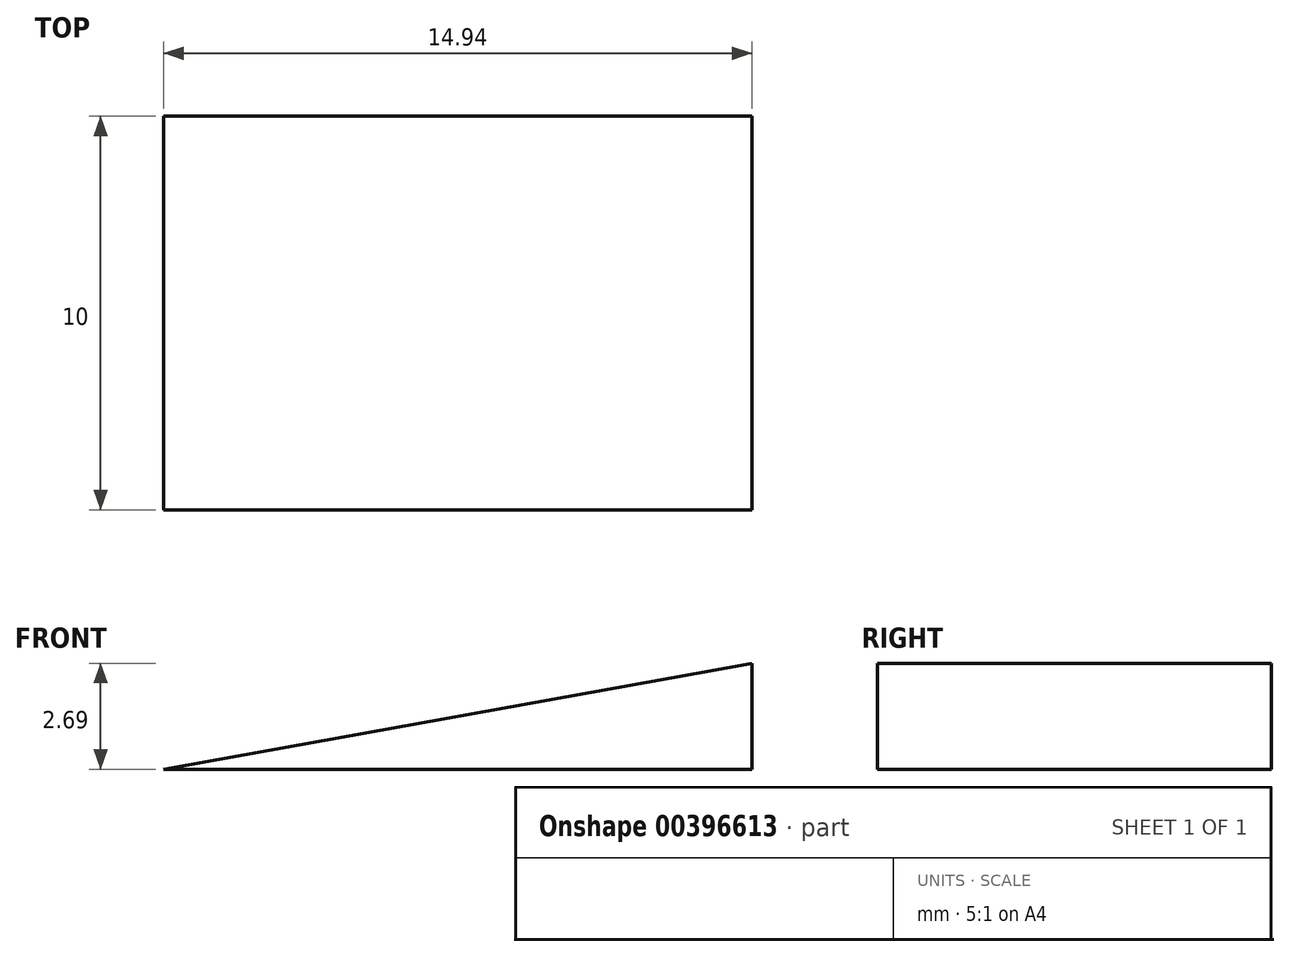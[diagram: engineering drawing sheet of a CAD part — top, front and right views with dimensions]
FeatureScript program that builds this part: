
annotation { "Feature Type Name" : "Feature", "Feature Type Description" : "" }
export const myFeature = defineFeature(function(context is Context, id is Id, definition is map)
    precondition{}
    {
        {
            var Q0;
            Q0=qCreatedBy(makeId("Front.planeOp"),FACE);
            var sketch = newSketch(context, id + "F0", { "sketchPlane" : qUnion([Q0])});
            skLineSegment(sketch, "E0", {"start": v(-14.94, 0) * mm, "end": v(0, 2.69) * mm});
            skLineSegment(sketch, "E1", {"start": v(0, 2.69) * mm, "end": v(0, 0) * mm});
            skLineSegment(sketch, "E2", {"start": v(0, 0) * mm, "end": v(-14.94, 0) * mm});
            skSolve(sketch);
        }
        {
            var Q0;
            Q0=makeQuery(id+"F0.imprint","IMPRINT",FACE,{"disambiguationData":[TD([[makeQuery(id+"F0.imprint","IMPRINT",EDGE,{"derivedFrom":sQuery(id+"F0.wireOp",EDGE,"E0")}),-1.0]])]});
            extrude(context, id + "F1", {"entities" : qUnion([Q0]), "depth" : 10 * mm});
        }
    });
